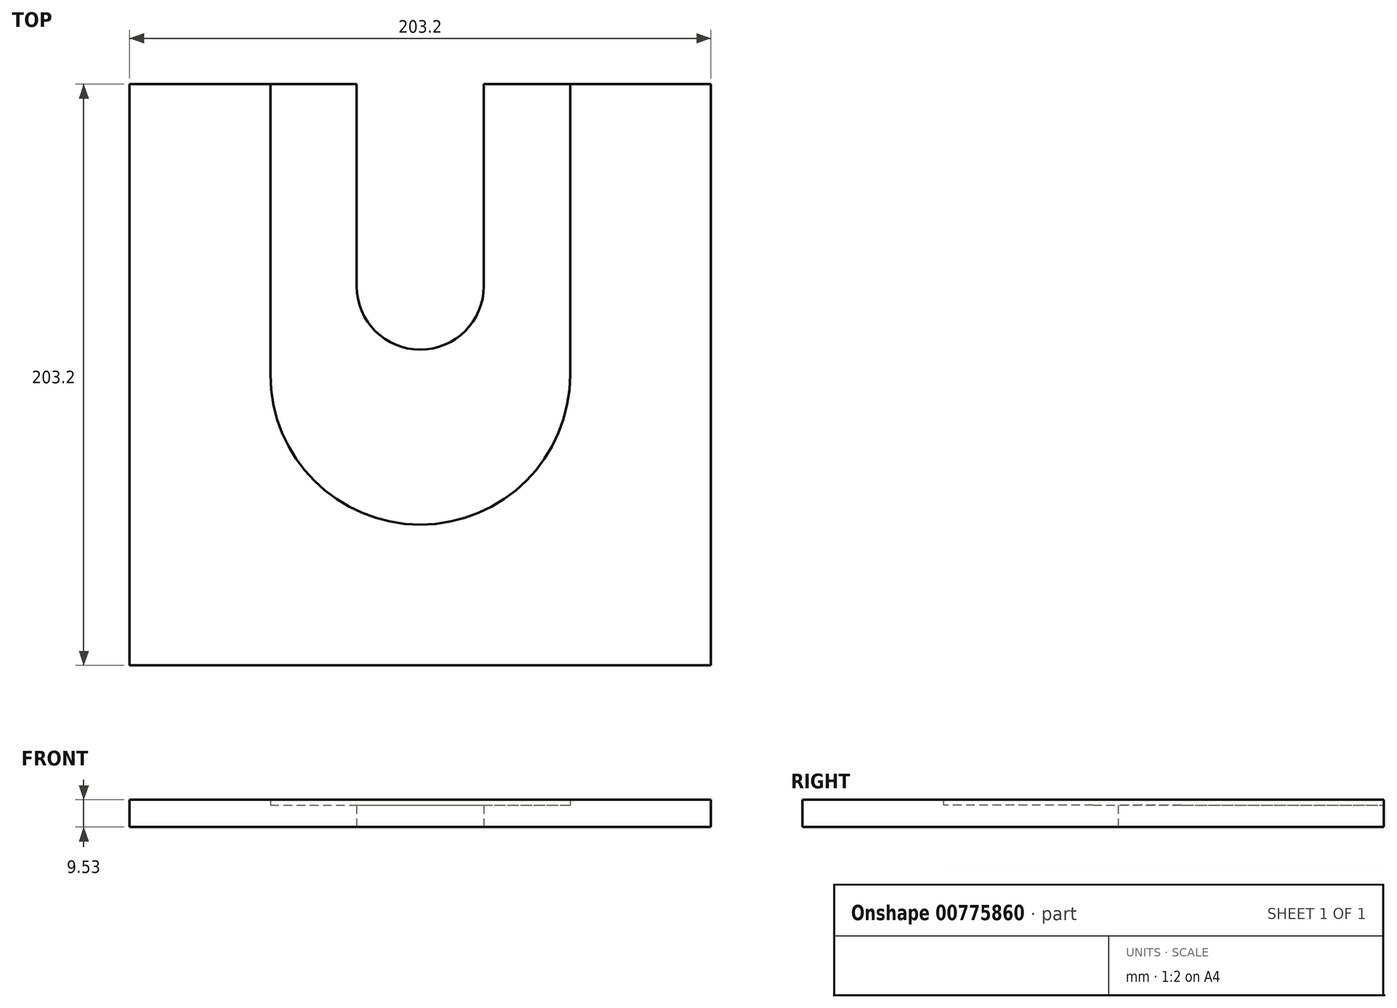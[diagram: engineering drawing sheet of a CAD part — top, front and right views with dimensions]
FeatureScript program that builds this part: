
annotation { "Feature Type Name" : "Feature", "Feature Type Description" : "" }
export const myFeature = defineFeature(function(context is Context, id is Id, definition is map)
    precondition{}
    {
        {
            var Q0;
            Q0=qCreatedBy(makeId("Top.planeOp"),FACE);
            var sketch = newSketch(context, id + "F0", { "sketchPlane" : qUnion([Q0])});
            skLineSegment(sketch, "E0.top", {"start": v(-101.6, -101.6) * mm, "end": v(101.6, -101.6) * mm});
            skLineSegment(sketch, "E0.left", {"start": v(-101.6, 101.6) * mm, "end": v(-101.6, -101.6) * mm});
            skLineSegment(sketch, "E0.right", {"start": v(101.6, 101.6) * mm, "end": v(101.6, -101.6) * mm});
            skPoint(sketch, "E0.middle", {"position": v(0, 0) * mm});
            skCircle(sketch, "E1", {"center": v(0, 0) * mm, "radius": 52.39 * mm});
            skLineSegment(sketch, "E2.bottom", {"start": v(-22.22, 31) * mm, "end": v(22.22, 31) * mm, "construction": true});
            skLineSegment(sketch, "E2.left", {"start": v(-22.22, 31) * mm, "end": v(-22.23, 101.6) * mm});
            skLineSegment(sketch, "E2.right", {"start": v(22.22, 31) * mm, "end": v(22.23, 101.6) * mm});
            skLineSegment(sketch, "E3", {"start": v(0, 0) * mm, "end": v(0, 31) * mm, "construction": true});
            skCircle(sketch, "E4", {"center": v(0, 31) * mm, "radius": 22.22 * mm});
            skLineSegment(sketch, "E5", {"start": v(-101.6, 101.6) * mm, "end": v(-22.23, 101.6) * mm});
            skLineSegment(sketch, "E6", {"start": v(22.23, 101.6) * mm, "end": v(101.6, 101.6) * mm});
            skLineSegment(sketch, "E7", {"start": v(-52.39, 0) * mm, "end": v(-52.39, 101.6) * mm});
            skLineSegment(sketch, "E8", {"start": v(52.39, 0) * mm, "end": v(52.39, 101.6) * mm});
            skSolve(sketch);
        }
        {
            var Q0;
            Q0=makeQuery(id+"F0.imprint","IMPRINT",FACE,{"disambiguationData":[TD([[makeQuery(id+"F0.imprint","IMPRINT",EDGE,{"derivedFrom":sQuery(id+"F0.wireOp",EDGE,"E0.top")}),1.0]])]});
            extrude(context, id + "F1", {"entities" : qUnion([Q0]), "depth" : 9.52 * mm, "offsetDistance" : 25.4 * mm});
        }
        {
            var Q0;
            {var subQ0=sQuery(id+"F0.wireOp",EDGE,"5RFHPdCz-Som7-NE5q-HNmN-mvt0QbCIfFGh");Q0=makeQuery(id+"F0.imprint","IMPRINT",FACE,{"disambiguationData":[TD([[makeQuery(id+"F0.imprint","IMPRINT",EDGE,{"derivedFrom":subQ0}),-1.0]])]});}
            var Q1;
            {var subQ0=sQuery(id+"F0.wireOp",EDGE,"E7");Q1=makeQuery(id+"F0.imprint","IMPRINT",FACE,{"disambiguationData":[TD([[makeQuery(id+"F0.imprint","IMPRINT",EDGE,{"derivedFrom":subQ0}),-1.0]])]});}
            var Q2;
            {var subQ0=sQuery(id+"F0.wireOp",EDGE,"E8");Q2=makeQuery(id+"F0.imprint","IMPRINT",FACE,{"disambiguationData":[TD([[makeQuery(id+"F0.imprint","IMPRINT",EDGE,{"derivedFrom":subQ0}),1.0]])]});}
            var Q3;
            {var subQ3=sQuery(id+"F0.wireOp",EDGE,"E1");var subQ6=makeQuery(id+"F0.imprint","INTERSECT",VERTEX,{"derivedFrom":[subQ3,sQuery(id+"F0.wireOp",EDGE,"E8")]});Q3=makeQuery(id+"F0.imprint","IMPRINT",FACE,{"disambiguationData":[TD([[makeQuery(id+"F0.imprint","IMPRINT",EDGE,{"disambiguationData":[TD([[subQ6,-1.0]])],"derivedFrom":subQ3}),1.0]])]});}
            extrude(context, id + "F2", {"entities" : qUnion([Q0, Q1, Q2, Q3]), "operationType" : NewBodyOperationType.ADD, "depth" : 7.62 * mm, "offsetDistance" : 25.4 * mm});
        }
    });
